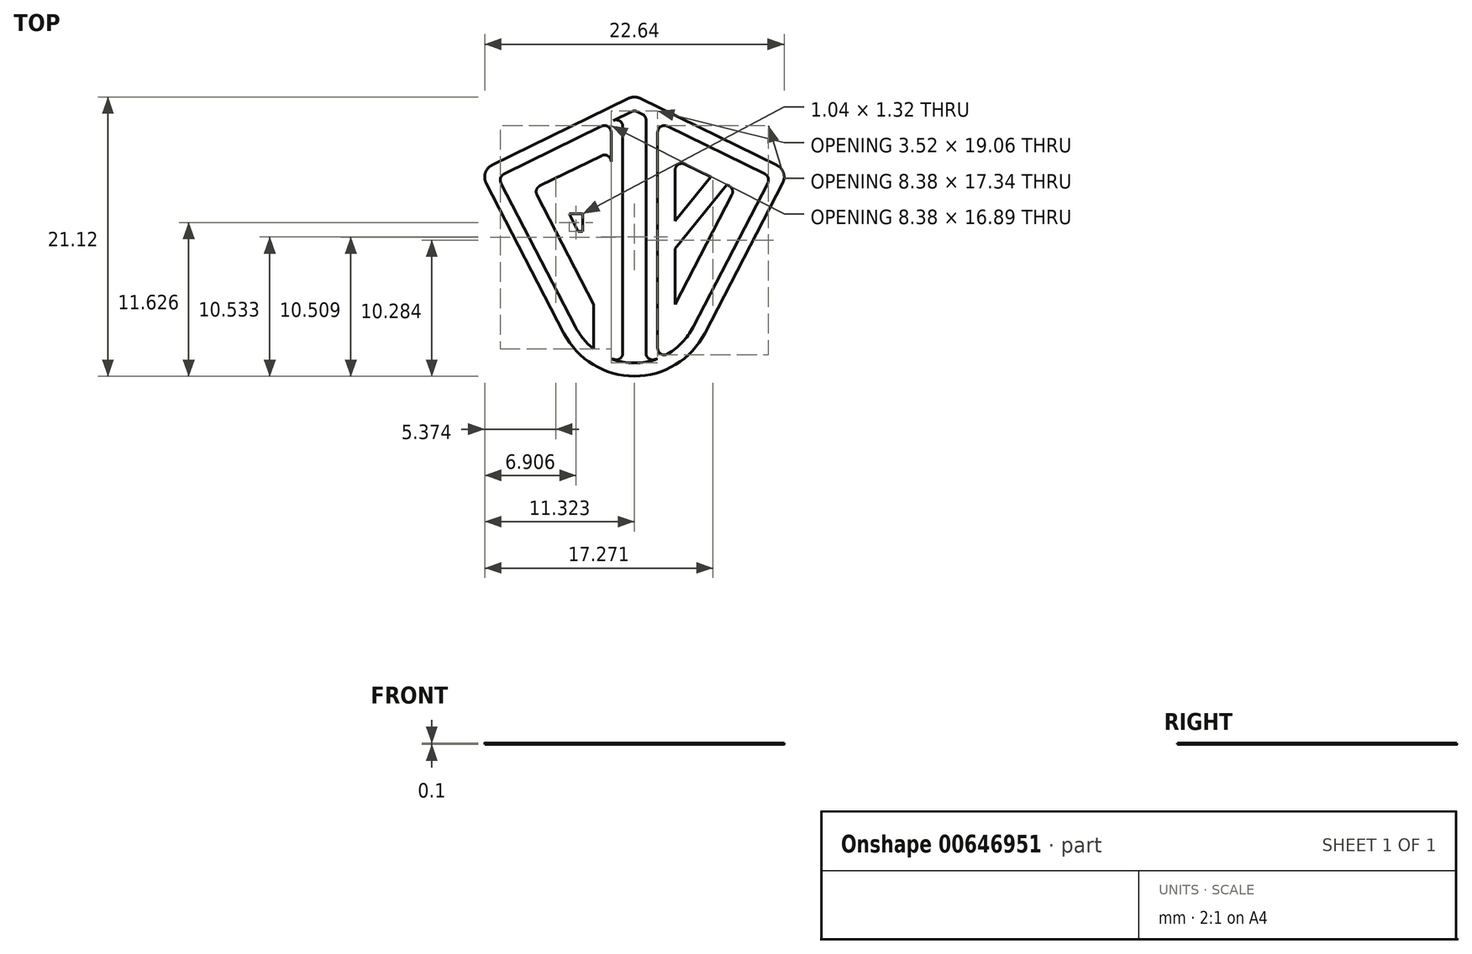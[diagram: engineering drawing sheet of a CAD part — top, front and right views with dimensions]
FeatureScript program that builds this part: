
annotation { "Feature Type Name" : "Feature", "Feature Type Description" : "" }
export const myFeature = defineFeature(function(context is Context, id is Id, definition is map)
    precondition{}
    {
        {
            var Q0;
            Q0=qCreatedBy(makeId("Top.planeOp"),FACE);
            var sketch = newSketch(context, id + "F0", { "sketchPlane" : qUnion([Q0])});
            skArc(sketch, "E0.MirrorCS", {"start": v(-12.62, 8.93) * mm, "mid": v(-12.18, 9.03) * mm, "end": v(-11.74, 8.93) * mm});
            skArc(sketch, "E1.MirrorCS", {"start": v(-1.42, 3.88) * mm, "mid": v(-0.9, 3.3) * mm, "end": v(-0.97, 2.52) * mm});
            skArc(sketch, "E2.MirrorCS", {"start": v(-23.38, 2.52) * mm, "mid": v(-23.45, 3.3) * mm, "end": v(-22.94, 3.88) * mm});
            skPoint(sketch, "E3.MirrorP", {"position": v(-23.85, 3.43) * mm});
            skArc(sketch, "E4.MirrorCS", {"start": v(-6.85, -8.84) * mm, "mid": v(-12.18, -12.09) * mm, "end": v(-17.5, -8.84) * mm});
            skLineSegment(sketch, "E5.MirrorCS", {"start": v(-6.85, -8.84) * mm, "end": v(-0.97, 2.52) * mm});
            skLineSegment(sketch, "E6.MirrorCS", {"start": v(-12.62, 8.93) * mm, "end": v(-22.94, 3.88) * mm});
            skLineSegment(sketch, "E7.MirrorCS", {"start": v(-23.38, 2.52) * mm, "end": v(-17.5, -8.84) * mm});
            skLineSegment(sketch, "E8.MirrorCS", {"start": v(-1.42, 3.88) * mm, "end": v(-11.74, 8.93) * mm});
            skLineSegment(sketch, "E9", {"start": v(-22.26, 2.53) * mm, "end": v(-16.62, -8.38) * mm});
            skArc(sketch, "E10.filletArc", {"start": v(-9.67, -10.41) * mm, "mid": v(-8.56, -9.53) * mm, "end": v(-7.74, -8.38) * mm});
            skLineSegment(sketch, "E11.MirrorCS", {"start": v(-10.42, 6.37) * mm, "end": v(-10.42, -9.98) * mm});
            skLineSegment(sketch, "E12.bottom", {"start": v(-15.25, 0.2) * mm, "end": v(-16.07, 0.2) * mm});
            skLineSegment(sketch, "E12.top", {"start": v(-15.75, -1.12) * mm, "end": v(-16.07, -1.12) * mm});
            skLineSegment(sketch, "E13", {"start": v(-15.25, 0.2) * mm, "end": v(-14.44, 0.2) * mm});
            skPoint(sketch, "E14", {"position": v(-16.57, -8.47) * mm});
            skPoint(sketch, "E15", {"position": v(-15.25, -10.03) * mm});
            skPoint(sketch, "E16", {"position": v(-13.94, -10.77) * mm});
            skPoint(sketch, "E17", {"position": v(-13.06, -11) * mm});
            skPoint(sketch, "E18", {"position": v(-11.3, -11) * mm});
            skPoint(sketch, "E19", {"position": v(-10.42, -10.77) * mm});
            skPoint(sketch, "E20", {"position": v(-9.1, -10.03) * mm});
            skPoint(sketch, "E21", {"position": v(-9.1, -6.67) * mm});
            skPoint(sketch, "E22", {"position": v(-2.78, 1.2) * mm});
            skPoint(sketch, "E23", {"position": v(-4.57, 2.08) * mm});
            skPoint(sketch, "E24", {"position": v(-9.1, 4.3) * mm});
            skPoint(sketch, "E25", {"position": v(-9.1, 6.52) * mm});
            skPoint(sketch, "E26", {"position": v(-10.42, 7.17) * mm});
            skPoint(sketch, "E27", {"position": v(-11.3, 7.6) * mm});
            skPoint(sketch, "E28", {"position": v(-13.06, 7.6) * mm});
            skPoint(sketch, "E29", {"position": v(-13.94, 7.17) * mm});
            skPoint(sketch, "E30", {"position": v(-15.25, 4.3) * mm});
            skPoint(sketch, "E31", {"position": v(-13.94, 4.94) * mm});
            skPoint(sketch, "E32", {"position": v(-13.06, 5.37) * mm});
            skPoint(sketch, "E33", {"position": v(-10.42, 4.94) * mm});
            skPoint(sketch, "E34", {"position": v(-11.3, 5.37) * mm});
            skPoint(sketch, "E35", {"position": v(-21.58, 1.2) * mm});
            skPoint(sketch, "E36", {"position": v(-19.78, 2.08) * mm});
            skPoint(sketch, "E37", {"position": v(-16.57, -4.12) * mm});
            skPoint(sketch, "E38", {"position": v(-16.57, -1.12) * mm});
            skPoint(sketch, "E39", {"position": v(-16.57, 0.2) * mm});
            skPoint(sketch, "E40", {"position": v(-15.25, 0.2) * mm});
            skPoint(sketch, "E41", {"position": v(-15.25, -1.12) * mm});
            skPoint(sketch, "E42", {"position": v(-13.94, 0.2) * mm});
            skLineSegment(sketch, "E43", {"start": v(-7.74, -8.38) * mm, "end": v(-2.78, 1.2) * mm});
            skLineSegment(sketch, "E44", {"start": v(-2.78, 1.2) * mm, "end": v(-2.1, 2.53) * mm});
            skLineSegment(sketch, "E45", {"start": v(-2.32, 3.2) * mm, "end": v(-9.1, 6.52) * mm});
            skLineSegment(sketch, "E46", {"start": v(-9.1, -6.67) * mm, "end": v(-4.8, 1.63) * mm});
            skLineSegment(sketch, "E47", {"start": v(-5.03, 2.3) * mm, "end": v(-8.38, 3.94) * mm});
            skLineSegment(sketch, "E48", {"start": v(-9.1, 3.5) * mm, "end": v(-9.1, -6.67) * mm});
            skLineSegment(sketch, "E49", {"start": v(-22.04, 3.2) * mm, "end": v(-14.65, 6.82) * mm});
            skLineSegment(sketch, "E50", {"start": v(-12.78, 7.74) * mm, "end": v(-12.4, 7.92) * mm});
            skLineSegment(sketch, "E51", {"start": v(-11.96, 7.92) * mm, "end": v(-11.58, 7.74) * mm});
            skLineSegment(sketch, "E52", {"start": v(-15.25, 4.3) * mm, "end": v(-19.32, 2.3) * mm});
            skLineSegment(sketch, "E53", {"start": v(-19.55, 1.63) * mm, "end": v(-16.57, -4.12) * mm});
            skLineSegment(sketch, "E54", {"start": v(-15.25, -1.62) * mm, "end": v(-15.25, -10.03) * mm});
            skPoint(sketch, "E55", {"position": v(-15.25, -6.67) * mm});
            skLineSegment(sketch, "E56", {"start": v(-16.57, -4.12) * mm, "end": v(-15.25, -6.67) * mm});
            skLineSegment(sketch, "E57", {"start": v(-15.25, 4.3) * mm, "end": v(-14.65, 4.59) * mm});
            skLineSegment(sketch, "E58", {"start": v(-9.1, 6.52) * mm, "end": v(-9.7, 6.82) * mm});
            skArc(sketch, "E59.filletArc", {"start": v(-22.04, 3.2) * mm, "mid": v(-22.3, 2.91) * mm, "end": v(-22.26, 2.53) * mm});
            skArc(sketch, "E60.filletArc", {"start": v(-2.1, 2.53) * mm, "mid": v(-2.06, 2.91) * mm, "end": v(-2.32, 3.2) * mm});
            skArc(sketch, "E61.filletArc", {"start": v(-13.94, 6.37) * mm, "mid": v(-14.17, 6.8) * mm, "end": v(-14.65, 6.82) * mm});
            skArc(sketch, "E62.filletArc", {"start": v(-9.7, 6.82) * mm, "mid": v(-10.18, 6.8) * mm, "end": v(-10.42, 6.37) * mm});
            skArc(sketch, "E63.filletArc", {"start": v(-8.38, 3.94) * mm, "mid": v(-8.87, 3.92) * mm, "end": v(-9.1, 3.5) * mm});
            skArc(sketch, "E64.filletArc", {"start": v(-4.8, 1.63) * mm, "mid": v(-4.78, 2.01) * mm, "end": v(-5.03, 2.3) * mm});
            skArc(sketch, "E65.filletArc", {"start": v(-19.32, 2.3) * mm, "mid": v(-19.58, 2.01) * mm, "end": v(-19.55, 1.63) * mm});
            skArc(sketch, "E66.filletArc", {"start": v(-13.94, 4.14) * mm, "mid": v(-14.17, 4.56) * mm, "end": v(-14.65, 4.59) * mm});
            skArc(sketch, "E67.filletArc", {"start": v(-15.25, -1.62) * mm, "mid": v(-15.4, -1.27) * mm, "end": v(-15.75, -1.12) * mm});
            skArc(sketch, "E68.filletArc", {"start": v(-13.94, -0.3) * mm, "mid": v(-14.08, 0.05) * mm, "end": v(-14.44, 0.2) * mm});
            skLineSegment(sketch, "E69", {"start": v(-13.94, 4.14) * mm, "end": v(-13.94, 6.37) * mm});
            skArc(sketch, "E70.filletArc", {"start": v(-11.96, 7.92) * mm, "mid": v(-12.18, 7.97) * mm, "end": v(-12.4, 7.92) * mm});
            skArc(sketch, "E71.filletArc", {"start": v(-12.78, 7.74) * mm, "mid": v(-12.98, 7.55) * mm, "end": v(-13.06, 7.29) * mm});
            skArc(sketch, "E72.filletArc", {"start": v(-11.3, 7.29) * mm, "mid": v(-11.37, 7.55) * mm, "end": v(-11.58, 7.74) * mm});
            skArc(sketch, "E73.filletArc", {"start": v(-10.42, -9.98) * mm, "mid": v(-10.17, -10.41) * mm, "end": v(-9.67, -10.41) * mm});
            skArc(sketch, "E74.MirrorCS", {"start": v(-14.69, -10.41) * mm, "mid": v(-15.8, -9.53) * mm, "end": v(-16.62, -8.38) * mm});
            skArc(sketch, "E75.MirrorCS", {"start": v(-13.94, -9.98) * mm, "mid": v(-14.19, -10.41) * mm, "end": v(-14.69, -10.41) * mm});
            skArc(sketch, "E76", {"start": v(-12.63, -11.1) * mm, "mid": v(-12.18, -11.14) * mm, "end": v(-11.72, -11.1) * mm});
            skLineSegment(sketch, "E77", {"start": v(-13.94, -9.98) * mm, "end": v(-13.94, -0.3) * mm});
            skLineSegment(sketch, "E78", {"start": v(-13.06, -10.61) * mm, "end": v(-13.06, 7.29) * mm});
            skLineSegment(sketch, "E79", {"start": v(-11.3, 7.29) * mm, "end": v(-11.3, -10.61) * mm});
            skArc(sketch, "E80.filletArc", {"start": v(-13.06, -10.61) * mm, "mid": v(-12.94, -10.94) * mm, "end": v(-12.63, -11.1) * mm});
            skArc(sketch, "E81.filletArc", {"start": v(-11.72, -11.1) * mm, "mid": v(-11.42, -10.94) * mm, "end": v(-11.3, -10.61) * mm});
            skPoint(sketch, "E82", {"position": v(-17.53, 0.99) * mm});
            skLineSegment(sketch, "E83", {"start": v(-16.07, 0.2) * mm, "end": v(-17.12, 0.2) * mm});
            skLineSegment(sketch, "E84", {"start": v(-16.07, -1.12) * mm, "end": v(-16.57, -1.12) * mm});
            skPoint(sketch, "E85", {"position": v(-16.43, -1.12) * mm});
            skLineSegment(sketch, "E86", {"start": v(-16.43, -1.12) * mm, "end": v(-17.12, 0.2) * mm});
            skLineSegment(sketch, "E87", {"start": v(-13.94, 7.17) * mm, "end": v(-13.78, 7.25) * mm});
            skLineSegment(sketch, "E88", {"start": v(-13.06, 5.37) * mm, "end": v(-13.06, 6.8) * mm});
            skArc(sketch, "E89.filletArc", {"start": v(-13.06, 6.8) * mm, "mid": v(-13.3, 7.22) * mm, "end": v(-13.78, 7.25) * mm});
            skLineSegment(sketch, "E90", {"start": v(-13.94, 7.17) * mm, "end": v(-12.78, 7.74) * mm});
            skLineSegment(sketch, "E91", {"start": v(-13.94, -10.77) * mm, "end": v(-13.69, -10.83) * mm});
            skLineSegment(sketch, "E92", {"start": v(-13.06, 5.37) * mm, "end": v(-13.06, -10.35) * mm});
            skArc(sketch, "E93.filletArc", {"start": v(-13.69, -10.83) * mm, "mid": v(-13.25, -10.75) * mm, "end": v(-13.06, -10.35) * mm});
            skLineSegment(sketch, "E94", {"start": v(-21.58, 1.2) * mm, "end": v(-16.62, -8.38) * mm});
            skLineSegment(sketch, "E95", {"start": v(-2.78, 1.2) * mm, "end": v(-7.74, -8.38) * mm});
            skArc(sketch, "E96.filletArc", {"start": v(-16.62, -8.38) * mm, "mid": v(-12.18, -11.09) * mm, "end": v(-7.74, -8.38) * mm});
            skLineSegment(sketch, "E97", {"start": v(-12.18, -8.2) * mm, "end": v(-12.18, -5.08) * mm});
            skArc(sketch, "E98.MirrorCS", {"start": v(-10.67, -10.83) * mm, "mid": v(-11.1, -10.75) * mm, "end": v(-11.3, -10.35) * mm});
            skLineSegment(sketch, "E99.MirrorCS", {"start": v(-10.42, -10.77) * mm, "end": v(-10.67, -10.83) * mm});
            skPoint(sketch, "E100", {"position": v(-9.1, -0.13) * mm});
            skPoint(sketch, "E101", {"position": v(-5.14, 2.36) * mm});
            skPoint(sketch, "E102", {"position": v(-4.77, 1.99) * mm});
            skPoint(sketch, "E103", {"position": v(-4.96, 1.34) * mm});
            skPoint(sketch, "E104", {"position": v(-9.1, -0.69) * mm});
            skPoint(sketch, "E105", {"position": v(-9.1, 0.42) * mm});
            skLineSegment(sketch, "E106", {"start": v(-16.07, -1.12) * mm, "end": v(-16.07, 0.2) * mm});
            skPoint(sketch, "E107", {"position": v(-5.47, 2.52) * mm});
            skPoint(sketch, "E108", {"position": v(-5.95, 2.75) * mm});
            skLineSegment(sketch, "E109", {"start": v(-6.06, 2.8) * mm, "end": v(-9.1, -1.23) * mm});
            skLineSegment(sketch, "E110", {"start": v(-6.06, 2.8) * mm, "end": v(-5.2, 2.39) * mm});
            skLineSegment(sketch, "E111", {"start": v(-5.2, 2.39) * mm, "end": v(-5.23, 2.36) * mm});
            skPoint(sketch, "E112", {"position": v(-9.1, 0.2) * mm});
            skPoint(sketch, "E113", {"position": v(-9.1, -1.12) * mm});
            skLineSegment(sketch, "E114", {"start": v(-9.1, -2.44) * mm, "end": v(-5.2, 2.39) * mm});
            skLineSegment(sketch, "E115", {"start": v(-6.06, 2.8) * mm, "end": v(-9.11, -0.97) * mm});
            skLineSegment(sketch, "E116", {"start": v(-6.75, 0.47) * mm, "end": v(-7.8, 1.26) * mm});
            skLineSegment(sketch, "E117", {"start": v(-7.8, 1.26) * mm, "end": v(-9.19, -0.58) * mm});
            skLineSegment(sketch, "E118", {"start": v(-9.19, -0.58) * mm, "end": v(-7.8, 1.26) * mm});
            skLineSegment(sketch, "E119", {"start": v(-7.8, 1.26) * mm, "end": v(-6.26, 3.17) * mm});
            skLineSegment(sketch, "E120", {"start": v(-7.8, 1.26) * mm, "end": v(-9.23, -0.5) * mm});
            skSolve(sketch);
        }
        {
            var Q0;
            {var subQ0=sQuery(id+"F0.wireOp",EDGE,"E46");Q0=makeQuery(id+"F0.imprint","IMPRINT",FACE,{"disambiguationData":[TD([[makeQuery(id+"F0.imprint","IMPRINT",EDGE,{"derivedFrom":subQ0}),1.0]])]});}
            var Q1;
            {var subQ0=sQuery(id+"F0.wireOp",EDGE,"E63.filletArc");Q1=makeQuery(id+"F0.imprint","IMPRINT",FACE,{"disambiguationData":[TD([[makeQuery(id+"F0.imprint","IMPRINT",EDGE,{"derivedFrom":subQ0}),1.0]])]});}
            var Q2;
            Q2=makeQuery(id+"F0.imprint","IMPRINT",FACE,{"disambiguationData":[TD([[makeQuery(id+"F0.imprint","IMPRINT",EDGE,{"derivedFrom":sQuery(id+"F0.wireOp",EDGE,"E0.MirrorCS")}),-1.0]])]});
            var Q3;
            {var subQ0=sQuery(id+"F0.wireOp",EDGE,"E76");Q3=makeQuery(id+"F0.imprint","IMPRINT",FACE,{"disambiguationData":[TD([[makeQuery(id+"F0.imprint","IMPRINT",EDGE,{"derivedFrom":subQ0}),1.0]])]});}
            var Q4;
            {var subQ3=sQuery(id+"F0.wireOp",EDGE,"RPIov1bO-qwDe-22lU-BV6p-ET71WXEMnufC");Q4=makeQuery(id+"F0.imprint","IMPRINT",FACE,{"disambiguationData":[TD([[makeQuery(id+"F0.imprint","IMPRINT",EDGE,{"derivedFrom":subQ3}),-1.0]])]});}
            var Q5;
            {var subQ5=sQuery(id+"F0.wireOp",EDGE,"E75.MirrorCS");Q5=makeQuery(id+"F0.imprint","IMPRINT",FACE,{"disambiguationData":[TD([[makeQuery(id+"F0.imprint","IMPRINT",EDGE,{"derivedFrom":subQ5}),1.0]])]});}
            var Q6;
            {var subQ1=sQuery(id+"F0.wireOp",EDGE,"E68.filletArc");Q6=makeQuery(id+"F0.imprint","IMPRINT",FACE,{"disambiguationData":[TD([[makeQuery(id+"F0.imprint","IMPRINT",EDGE,{"derivedFrom":subQ1}),-1.0]])]});}
            var Q7;
            {var subQ1=sQuery(id+"F0.wireOp",EDGE,"E73.filletArc");Q7=makeQuery(id+"F0.imprint","IMPRINT",FACE,{"disambiguationData":[TD([[makeQuery(id+"F0.imprint","IMPRINT",EDGE,{"derivedFrom":subQ1}),-1.0]])]});}
            var Q8;
            {var subQ0=sQuery(id+"F0.wireOp",EDGE,"Cl3IQgta-nqtW-K0ye-efcI-YpJCdKnWrlVx");var subQ1=sQuery(id+"F0.wireOp",EDGE,"E11.MirrorCS");var subQ2=makeQuery(id+"F0.imprint","INTERSECT",VERTEX,{"derivedFrom":[subQ1,subQ0]});Q8=makeQuery(id+"F0.imprint","IMPRINT",FACE,{"disambiguationData":[TD([[makeQuery(id+"F0.imprint","IMPRINT",EDGE,{"disambiguationData":[TD([[subQ2,-1.0]])],"derivedFrom":subQ1}),-1.0]])]});}
            var Q9;
            {var subQ0=sQuery(id+"F0.wireOp",EDGE,"E48");var subQ1=sQuery(id+"F0.wireOp",EDGE,"E46");var subQ2=makeQuery(id+"F0.imprint","INTERSECT",VERTEX,{"derivedFrom":[subQ1,subQ0]});Q9=makeQuery(id+"F0.imprint","IMPRINT",FACE,{"disambiguationData":[TD([[makeQuery(id+"F0.imprint","IMPRINT",EDGE,{"disambiguationData":[TD([[subQ2,-1.0]])],"derivedFrom":subQ1}),1.0]])]});}
            var Q10;
            {var subQ0=sQuery(id+"F0.wireOp",EDGE,"tmzpQr5O-wWc1-ln0N-NPHb-jfIugI6lGER6");var subQ1=sQuery(id+"F0.wireOp",EDGE,"w3vRnku4-Teg6-SXiI-nqO1-kFEqONE9hBVN");var subQ2=makeQuery(id+"F0.imprint","INTERSECT",VERTEX,{"derivedFrom":[subQ1,subQ0]});Q10=makeQuery(id+"F0.imprint","IMPRINT",FACE,{"disambiguationData":[TD([[makeQuery(id+"F0.imprint","IMPRINT",EDGE,{"disambiguationData":[TD([[subQ2,-1.0]])],"derivedFrom":subQ1}),1.0]])]});}
            var Q11;
            {var subQ1=sQuery(id+"F0.wireOp",EDGE,"E46");var subQ5=sQuery(id+"F0.wireOp",EDGE,"Cl3IQgta-nqtW-K0ye-efcI-YpJCdKnWrlVx");var subQ6=makeQuery(id+"F0.imprint","INTERSECT",VERTEX,{"derivedFrom":[subQ1,subQ5]});Q11=makeQuery(id+"F0.imprint","IMPRINT",FACE,{"disambiguationData":[TD([[makeQuery(id+"F0.imprint","IMPRINT",EDGE,{"disambiguationData":[TD([[subQ6,1.0]])],"derivedFrom":subQ1}),1.0]])]});}
            var Q12;
            {var subQ0=sQuery(id+"F0.wireOp",EDGE,"E111");Q12=makeQuery(id+"F0.imprint","IMPRINT",FACE,{"disambiguationData":[TD([[makeQuery(id+"F0.imprint","IMPRINT",EDGE,{"derivedFrom":subQ0}),1.0]])]});}
            var Q13;
            {var subQ0=sQuery(id+"F0.wireOp",EDGE,"tmzpQr5O-wWc1-ln0N-NPHb-jfIugI6lGER6");var subQ1=sQuery(id+"F0.wireOp",EDGE,"E11.MirrorCS");var subQ2=makeQuery(id+"F0.imprint","INTERSECT",VERTEX,{"derivedFrom":[subQ1,subQ0]});Q13=makeQuery(id+"F0.imprint","IMPRINT",FACE,{"disambiguationData":[TD([[makeQuery(id+"F0.imprint","IMPRINT",EDGE,{"disambiguationData":[TD([[subQ2,-1.0]])],"derivedFrom":subQ1}),-1.0]])]});}
            var Q14;
            {var subQ0=sQuery(id+"F0.wireOp",EDGE,"afa05864-eb28-49e8-95be-b6718b75a2b20.MirrorCS");var subQ1=sQuery(id+"F0.wireOp",EDGE,"E77");var subQ2=makeQuery(id+"F0.imprint","INTERSECT",VERTEX,{"derivedFrom":[subQ1,subQ0]});Q14=makeQuery(id+"F0.imprint","IMPRINT",FACE,{"disambiguationData":[TD([[makeQuery(id+"F0.imprint","IMPRINT",EDGE,{"disambiguationData":[TD([[subQ2,-1.0]])],"derivedFrom":subQ1}),-1.0]])]});}
            var Q15;
            {var subQ5=sQuery(id+"F0.wireOp",EDGE,"E47");var subQ7=sQuery(id+"F0.wireOp",EDGE,"a02aedb6-8c73-418c-b080-1dd0916ab2010.MirrorCS");var subQ9=makeQuery(id+"F0.imprint","INTERSECT",VERTEX,{"derivedFrom":[subQ5,subQ7]});Q15=makeQuery(id+"F0.imprint","IMPRINT",FACE,{"disambiguationData":[TD([[makeQuery(id+"F0.imprint","IMPRINT",EDGE,{"disambiguationData":[TD([[subQ9,1.0]])],"derivedFrom":subQ7}),-1.0]])]});}
            var Q16;
            {var subQ0=sQuery(id+"F0.wireOp",EDGE,"afa05864-eb28-49e8-95be-b6718b75a2b20.MirrorCS");var subQ1=sQuery(id+"F0.wireOp",EDGE,"w3vRnku4-Teg6-SXiI-nqO1-kFEqONE9hBVN");var subQ2=makeQuery(id+"F0.imprint","INTERSECT",VERTEX,{"derivedFrom":[subQ1,subQ0]});Q16=makeQuery(id+"F0.imprint","IMPRINT",FACE,{"disambiguationData":[TD([[makeQuery(id+"F0.imprint","IMPRINT",EDGE,{"disambiguationData":[TD([[subQ2,-1.0]])],"derivedFrom":subQ1}),1.0]])]});}
            var Q17;
            {var subQ5=sQuery(id+"F0.wireOp",EDGE,"E64.filletArc");var subQ6=sQuery(id+"F0.wireOp",EDGE,"E46");var subQ7=makeQuery(id+"F0.imprint","INTERSECT",VERTEX,{"derivedFrom":[subQ6,subQ5]});Q17=makeQuery(id+"F0.imprint","IMPRINT",FACE,{"disambiguationData":[TD([[makeQuery(id+"F0.imprint","IMPRINT",EDGE,{"disambiguationData":[TD([[subQ7,1.0]])],"derivedFrom":subQ6}),1.0]])]});}
            var Q18;
            {var subQ1=sQuery(id+"F0.wireOp",EDGE,"E64.filletArc");var subQ7=sQuery(id+"F0.wireOp",EDGE,"E47");var subQ8=makeQuery(id+"F0.imprint","INTERSECT",VERTEX,{"derivedFrom":[subQ7,subQ1]});Q18=makeQuery(id+"F0.imprint","IMPRINT",FACE,{"disambiguationData":[TD([[makeQuery(id+"F0.imprint","IMPRINT",EDGE,{"disambiguationData":[TD([[subQ8,1.0]])],"derivedFrom":subQ1}),1.0]])]});}
            var Q19;
            {var subQ0=sQuery(id+"F0.wireOp",EDGE,"SzZBVxO3-oEJs-8OU1-3VI5-5WsEBxKBmkIE");var subQ1=sQuery(id+"F0.wireOp",EDGE,"w3vRnku4-Teg6-SXiI-nqO1-kFEqONE9hBVN");var subQ2=makeQuery(id+"F0.imprint","INTERSECT",VERTEX,{"derivedFrom":[subQ1,subQ0]});Q19=makeQuery(id+"F0.imprint","IMPRINT",FACE,{"disambiguationData":[TD([[makeQuery(id+"F0.imprint","IMPRINT",EDGE,{"disambiguationData":[TD([[subQ2,-1.0]])],"derivedFrom":subQ1}),1.0]])]});}
            var Q20;
            {var subQ0=sQuery(id+"F0.wireOp",EDGE,"Cl3IQgta-nqtW-K0ye-efcI-YpJCdKnWrlVx");var subQ1=sQuery(id+"F0.wireOp",EDGE,"w3vRnku4-Teg6-SXiI-nqO1-kFEqONE9hBVN");var subQ2=makeQuery(id+"F0.imprint","INTERSECT",VERTEX,{"derivedFrom":[subQ1,subQ0]});Q20=makeQuery(id+"F0.imprint","IMPRINT",FACE,{"disambiguationData":[TD([[makeQuery(id+"F0.imprint","IMPRINT",EDGE,{"disambiguationData":[TD([[subQ2,-1.0]])],"derivedFrom":subQ1}),1.0]])]});}
            var Q21;
            {var subQ0=sQuery(id+"F0.wireOp",EDGE,"SzZBVxO3-oEJs-8OU1-3VI5-5WsEBxKBmkIE");var subQ1=sQuery(id+"F0.wireOp",EDGE,"w3vRnku4-Teg6-SXiI-nqO1-kFEqONE9hBVN");var subQ2=makeQuery(id+"F0.imprint","INTERSECT",VERTEX,{"derivedFrom":[subQ1,subQ0]});Q21=makeQuery(id+"F0.imprint","IMPRINT",FACE,{"disambiguationData":[TD([[makeQuery(id+"F0.imprint","IMPRINT",EDGE,{"disambiguationData":[TD([[subQ2,-1.0]])],"derivedFrom":subQ1}),-1.0]])]});}
            var Q22;
            {var subQ0=sQuery(id+"F0.wireOp",EDGE,"afa05864-eb28-49e8-95be-b6718b75a2b20.MirrorCS");var subQ1=sQuery(id+"F0.wireOp",EDGE,"E46");var subQ2=makeQuery(id+"F0.imprint","INTERSECT",VERTEX,{"derivedFrom":[subQ1,subQ0]});Q22=makeQuery(id+"F0.imprint","IMPRINT",FACE,{"disambiguationData":[TD([[makeQuery(id+"F0.imprint","IMPRINT",EDGE,{"disambiguationData":[TD([[subQ2,-1.0]])],"derivedFrom":subQ1}),1.0]])]});}
            extrude(context, id + "F1", {"entities" : qUnion([Q0, Q1, Q2, Q3, Q4, Q5, Q6, Q7, Q8, Q9, Q10, Q11, Q12, Q13, Q14, Q15, Q16, Q17, Q18, Q19, Q20, Q21, Q22]), "depth" : .1 * mm, "offsetDistance" : 25 * mm});
        }
    });
